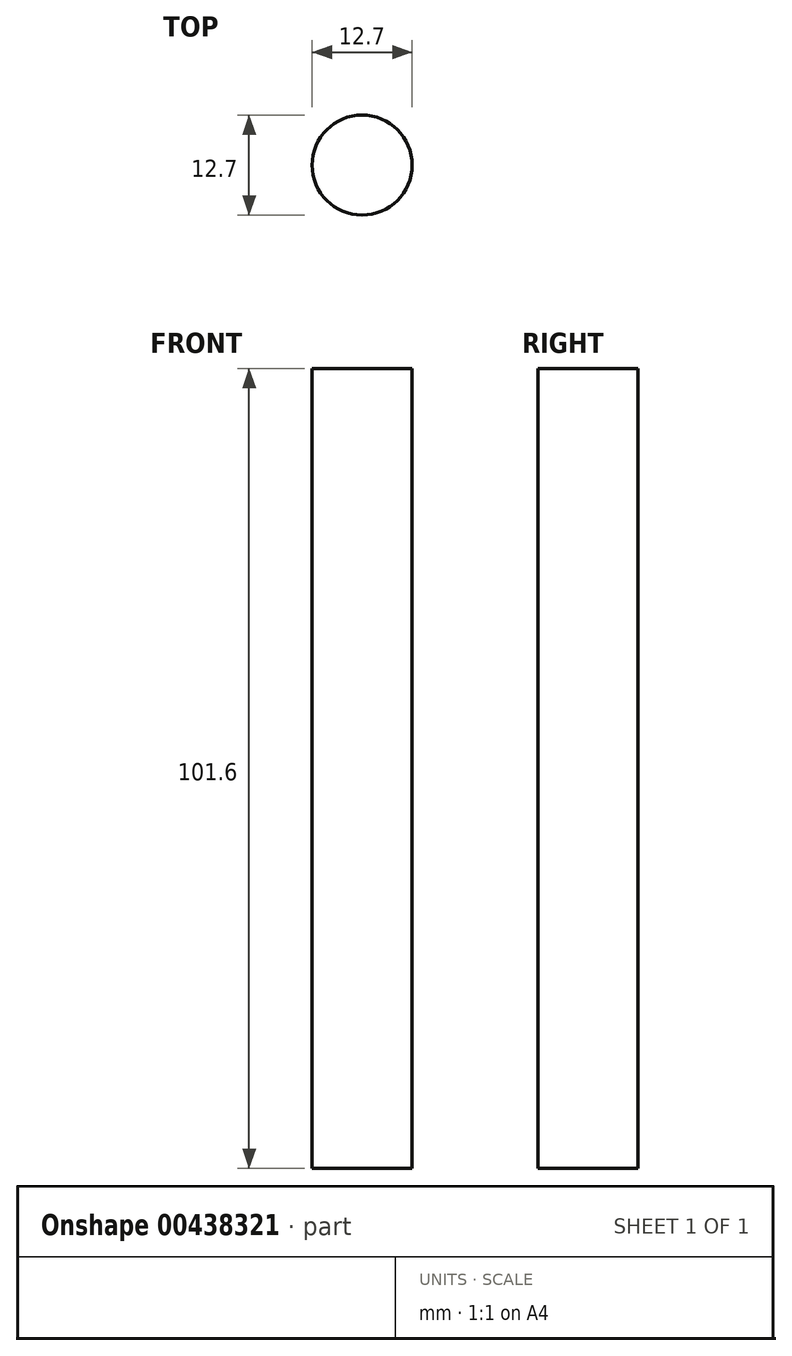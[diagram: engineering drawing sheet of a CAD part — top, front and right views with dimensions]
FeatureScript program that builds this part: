
annotation { "Feature Type Name" : "Feature", "Feature Type Description" : "" }
export const myFeature = defineFeature(function(context is Context, id is Id, definition is map)
    precondition{}
    {
        {
            var Q0;
            Q0=qCreatedBy(makeId("Top.planeOp"),FACE);
            var sketch = newSketch(context, id + "F0", { "sketchPlane" : qUnion([Q0])});
            skCircle(sketch, "E0", {"center": v(0, 0) * mm, "radius": 6.35 * mm});
            skSolve(sketch);
        }
        {
            var Q0;
            Q0=makeQuery(id+"F0.imprint","IMPRINT",FACE,{"disambiguationData":[TD([[makeQuery(id+"F0.imprint","IMPRINT",EDGE,{"derivedFrom":sQuery(id+"F0.wireOp",EDGE,"E0")}),1.0]])]});
            extrude(context, id + "F1", {"entities" : qUnion([Q0]), "depth" : 101.6 * mm});
        }
    });
